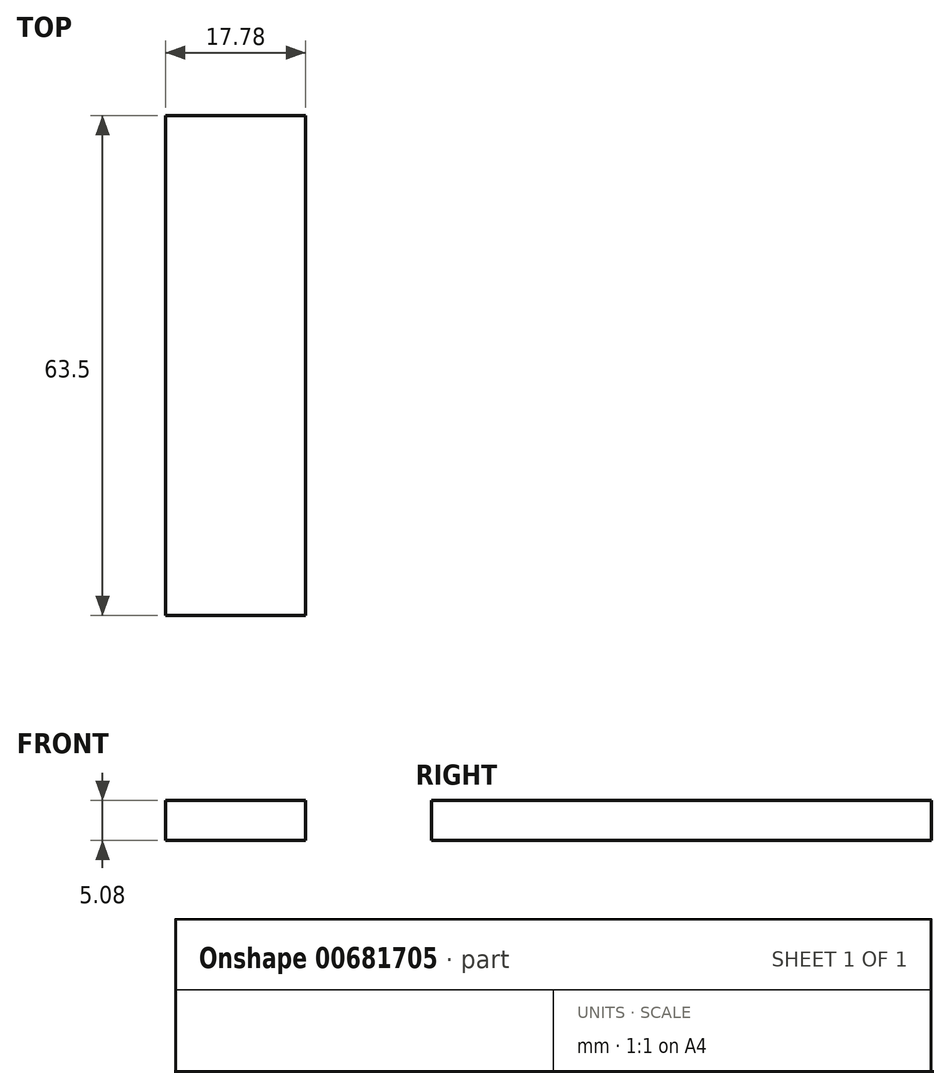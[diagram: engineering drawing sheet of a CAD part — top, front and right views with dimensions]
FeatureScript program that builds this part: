
annotation { "Feature Type Name" : "Feature", "Feature Type Description" : "" }
export const myFeature = defineFeature(function(context is Context, id is Id, definition is map)
    precondition{}
    {
        {
            var Q0;
            Q0=qCreatedBy(makeId("Top.planeOp"),FACE);
            var sketch = newSketch(context, id + "F0", { "sketchPlane" : qUnion([Q0])});
            skLineSegment(sketch, "E0.bottom", {"start": v(-17.78, 71.81) * mm, "end": v(0, 71.81) * mm});
            skLineSegment(sketch, "E0.top", {"start": v(-17.78, 8.31) * mm, "end": v(0, 8.31) * mm});
            skLineSegment(sketch, "E0.left", {"start": v(-17.78, 71.81) * mm, "end": v(-17.78, 8.31) * mm});
            skLineSegment(sketch, "E0.right", {"start": v(0, 71.81) * mm, "end": v(0, 8.31) * mm});
            skSolve(sketch);
        }
        {
            var Q0;
            Q0=makeQuery(id+"F0.imprint","IMPRINT",FACE,{"disambiguationData":[TD([[makeQuery(id+"F0.imprint","IMPRINT",EDGE,{"derivedFrom":sQuery(id+"F0.wireOp",EDGE,"E0.bottom")}),-1.0]])]});
            extrude(context, id + "F1", {"entities" : qUnion([Q0]), "depth" : 5.08 * mm, "offsetDistance" : 25.4 * mm});
        }
    });
